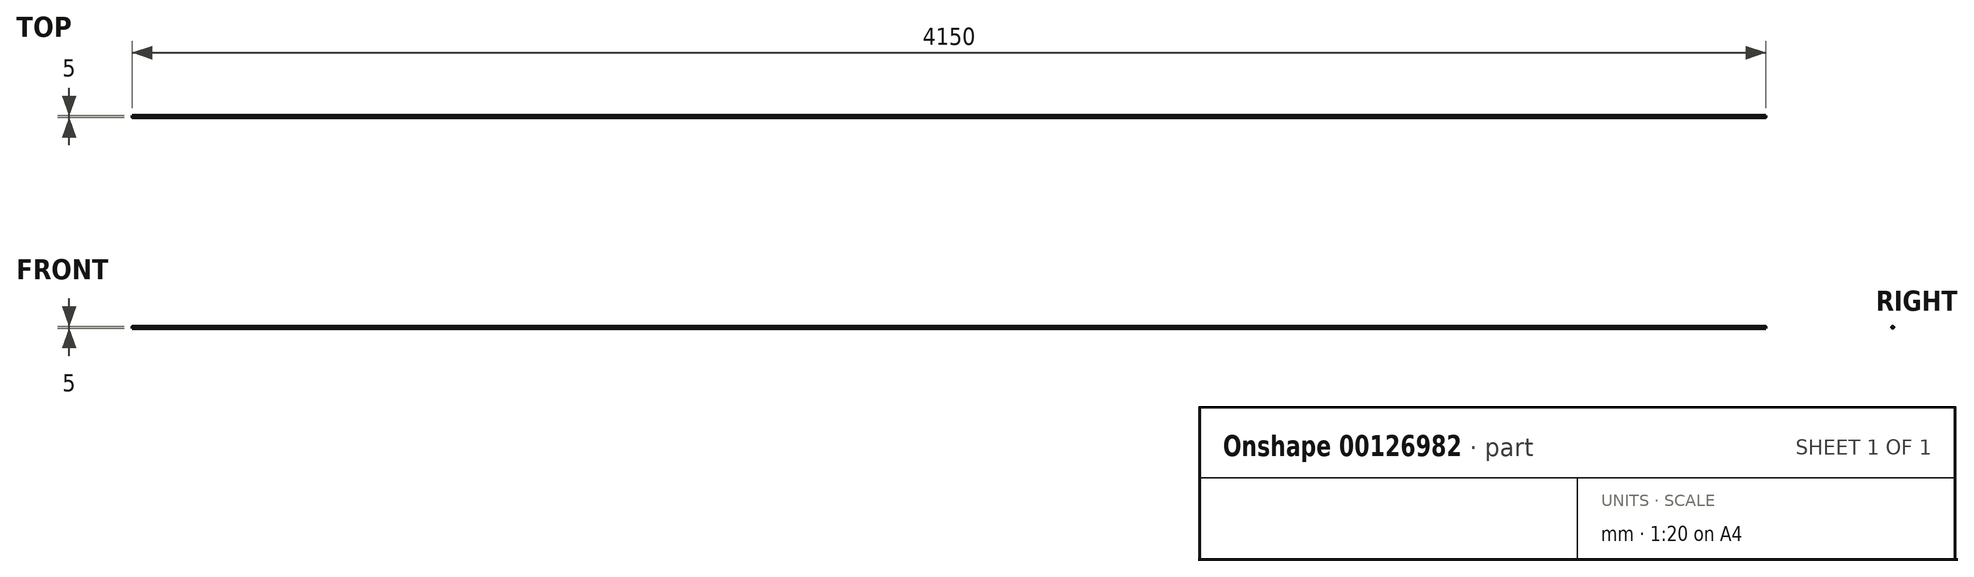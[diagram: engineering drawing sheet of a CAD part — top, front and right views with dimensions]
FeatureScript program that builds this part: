
annotation { "Feature Type Name" : "Feature", "Feature Type Description" : "" }
export const myFeature = defineFeature(function(context is Context, id is Id, definition is map)
    precondition{}
    {
        {
            var Q0;
            Q0=qCreatedBy(makeId("Right.planeOp"),FACE);
            var sketch = newSketch(context, id + "F0", { "sketchPlane" : qUnion([Q0])});
            skCircle(sketch, "E0", {"center": v(0, 0) * mm, "radius": 2.5 * mm});
            skSolve(sketch);
        }
        {
            var Q0;
            Q0 = qSketchRegion(id + "F0", true);
            extrude(context, id + "F1", {"entities" : qUnion([Q0]), "depth" : 4150 * mm});
        }
    });
